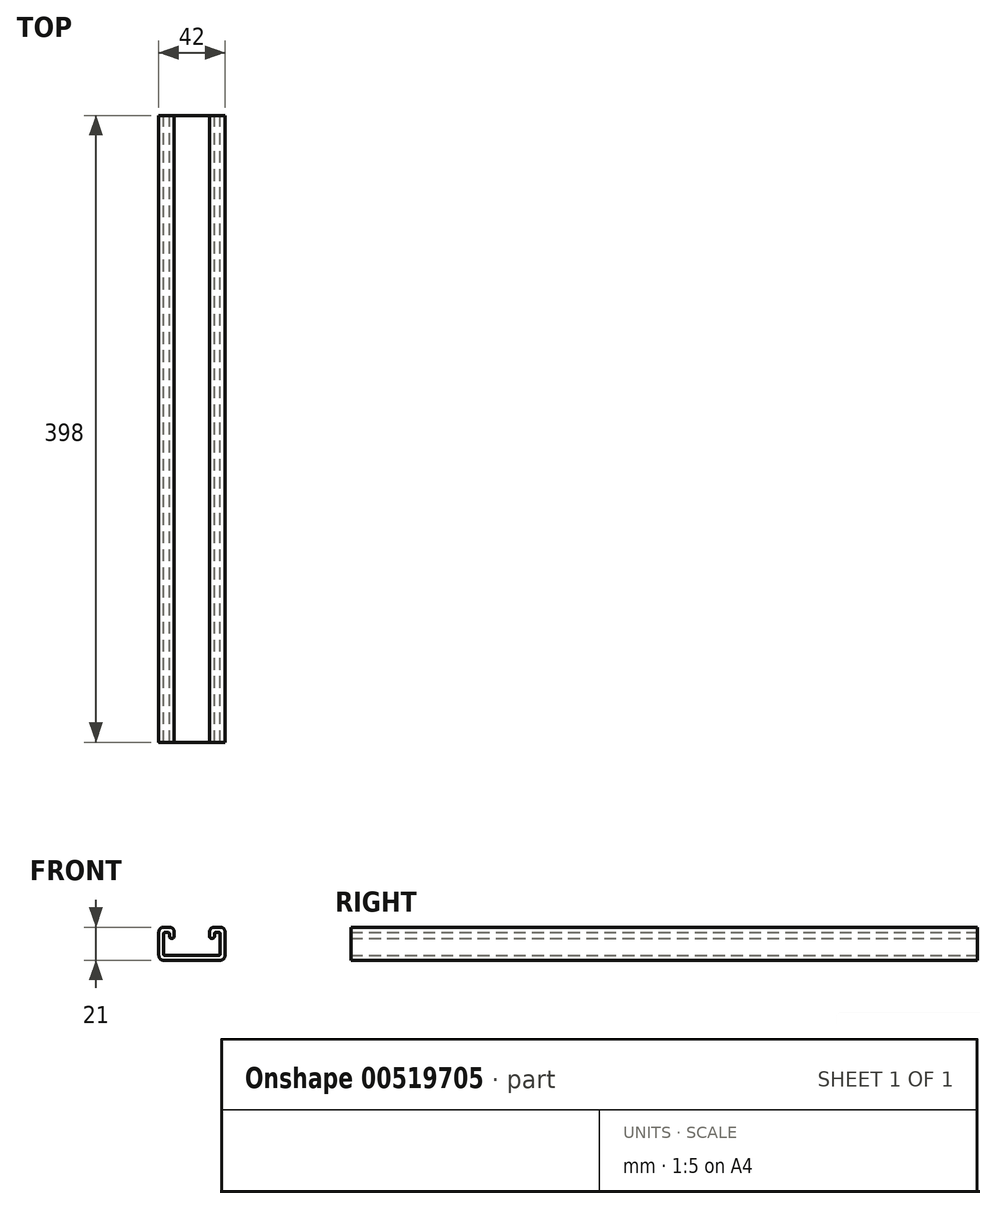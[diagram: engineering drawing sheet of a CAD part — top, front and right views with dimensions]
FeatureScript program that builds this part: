
annotation { "Feature Type Name" : "Feature", "Feature Type Description" : "" }
export const myFeature = defineFeature(function(context is Context, id is Id, definition is map)
    precondition{}
    {
        {
            var Q0;
            Q0=qCreatedBy(makeId("Front.planeOp"),FACE);
            var sketch = newSketch(context, id + "F0", { "sketchPlane" : qUnion([Q0])});
            skLineSegment(sketch, "E0.bottom", {"start": v(0, 0) * mm, "end": v(42, 0) * mm});
            skLineSegment(sketch, "E0.top", {"start": v(0, 21) * mm, "end": v(42, 21) * mm});
            skLineSegment(sketch, "E0.left", {"start": v(0, 0) * mm, "end": v(0, 21) * mm});
            skLineSegment(sketch, "E0.right", {"start": v(42, 0) * mm, "end": v(42, 21) * mm});
            skLineSegment(sketch, "E1.bottom", {"start": v(3, 3) * mm, "end": v(39, 3) * mm});
            skLineSegment(sketch, "E1.top", {"start": v(3, 14) * mm, "end": v(39, 14) * mm});
            skLineSegment(sketch, "E1.left", {"start": v(3, 3) * mm, "end": v(3, 14) * mm});
            skLineSegment(sketch, "E1.right", {"start": v(39, 3) * mm, "end": v(39, 14) * mm});
            skLineSegment(sketch, "E2.bottom", {"start": v(9.75, 21) * mm, "end": v(32.25, 21) * mm});
            skLineSegment(sketch, "E2.top", {"start": v(9.75, 14) * mm, "end": v(32.25, 14) * mm});
            skLineSegment(sketch, "E2.left", {"start": v(9.75, 21) * mm, "end": v(9.75, 14) * mm});
            skLineSegment(sketch, "E2.right", {"start": v(32.25, 21) * mm, "end": v(32.25, 14) * mm});
            skLineSegment(sketch, "E3.bottom", {"start": v(3.02, 17.75) * mm, "end": v(6.77, 17.75) * mm});
            skLineSegment(sketch, "E3.top", {"start": v(3.02, 14) * mm, "end": v(6.77, 14) * mm});
            skLineSegment(sketch, "E3.left", {"start": v(3.02, 17.75) * mm, "end": v(3.02, 14) * mm});
            skLineSegment(sketch, "E3.right", {"start": v(6.77, 17.75) * mm, "end": v(6.77, 14) * mm});
            skLineSegment(sketch, "E4.bottom", {"start": v(35.25, 17.75) * mm, "end": v(39, 17.75) * mm});
            skLineSegment(sketch, "E4.top", {"start": v(35.25, 14) * mm, "end": v(39, 14) * mm});
            skLineSegment(sketch, "E4.left", {"start": v(35.25, 17.75) * mm, "end": v(35.25, 14) * mm});
            skLineSegment(sketch, "E4.right", {"start": v(39, 17.75) * mm, "end": v(39, 14) * mm});
            skSolve(sketch);
        }
        {
            var Q0;
            Q0=makeQuery(id+"F0.imprint","IMPRINT",FACE,{"disambiguationData":[TD([[makeQuery(id+"F0.imprint","IMPRINT",EDGE,{"derivedFrom":sQuery(id+"F0.wireOp",EDGE,"E0.bottom")}),1.0]])]});
            extrude(context, id + "F1", {"entities" : qUnion([Q0]), "depth" : 398 * mm, "offsetDistance" : 25 * mm});
        }
        {
            var Q0;
            Q0=makeQuery(id+"F1.opExtrude","SWEPT_EDGE",EDGE,{"disambiguationData":[OSD([sQuery(id+"F0.wireOp",EDGE,"E0.top"),sQuery(id+"F0.wireOp",EDGE,"E0.left")])]});
            var Q1;
            Q1=makeQuery(id+"F1.opExtrude","SWEPT_EDGE",EDGE,{"disambiguationData":[OSD([sQuery(id+"F0.wireOp",EDGE,"E0.top"),sQuery(id+"F0.wireOp",EDGE,"E2.bottom"),sQuery(id+"F0.wireOp",EDGE,"E2.left")])]});
            var Q2;
            Q2=makeQuery(id+"F1.opExtrude","SWEPT_EDGE",EDGE,{"disambiguationData":[OSD([sQuery(id+"F0.wireOp",EDGE,"E0.top"),sQuery(id+"F0.wireOp",EDGE,"E2.bottom"),sQuery(id+"F0.wireOp",EDGE,"E2.right")])]});
            var Q3;
            Q3=makeQuery(id+"F1.opExtrude","SWEPT_EDGE",EDGE,{"disambiguationData":[OSD([sQuery(id+"F0.wireOp",EDGE,"E0.top"),sQuery(id+"F0.wireOp",EDGE,"E0.right")])]});
            var Q4;
            Q4=makeQuery(id+"F1.opExtrude","SWEPT_EDGE",EDGE,{"disambiguationData":[OSD([sQuery(id+"F0.wireOp",EDGE,"E0.bottom"),sQuery(id+"F0.wireOp",EDGE,"E0.left")])]});
            var Q5;
            Q5=makeQuery(id+"F1.opExtrude","SWEPT_EDGE",EDGE,{"disambiguationData":[OSD([sQuery(id+"F0.wireOp",EDGE,"E0.bottom"),sQuery(id+"F0.wireOp",EDGE,"E0.right")])]});
            fillet(context, id + "F2", {"entities" : qUnion([Q0, Q1, Q2, Q3, Q4, Q5]), "radius" : 3 * mm, "tangentPropagation" : true, "allowEdgeOverflow" : false});
        }
        {
            var Q0;
            Q0=makeQuery(id+"F1.opExtrude","SWEPT_EDGE",EDGE,{"disambiguationData":[OSD([sQuery(id+"F0.wireOp",EDGE,"E1.top"),sQuery(id+"F0.wireOp",EDGE,"E3.top"),sQuery(id+"F0.wireOp",EDGE,"E3.right")])]});
            var Q1;
            Q1=makeQuery(id+"F1.opExtrude","SWEPT_EDGE",EDGE,{"disambiguationData":[OSD([sQuery(id+"F0.wireOp",EDGE,"E1.top"),sQuery(id+"F0.wireOp",EDGE,"E2.top"),sQuery(id+"F0.wireOp",EDGE,"E2.right")])]});
            var Q2;
            Q2=makeQuery(id+"F1.opExtrude","SWEPT_EDGE",EDGE,{"disambiguationData":[OSD([sQuery(id+"F0.wireOp",EDGE,"E1.top"),sQuery(id+"F0.wireOp",EDGE,"E4.top"),sQuery(id+"F0.wireOp",EDGE,"E4.left")])]});
            var Q3;
            Q3=makeQuery(id+"F1.opExtrude","SWEPT_EDGE",EDGE,{"disambiguationData":[OSD([sQuery(id+"F0.wireOp",EDGE,"E1.top"),sQuery(id+"F0.wireOp",EDGE,"E2.top"),sQuery(id+"F0.wireOp",EDGE,"E2.left")])]});
            var Q4;
            Q4=makeQuery(id+"F1.opExtrude","SWEPT_EDGE",EDGE,{"disambiguationData":[OSD([sQuery(id+"F0.wireOp",EDGE,"E1.bottom"),sQuery(id+"F0.wireOp",EDGE,"E1.left")])]});
            var Q5;
            Q5=makeQuery(id+"F1.opExtrude","SWEPT_EDGE",EDGE,{"disambiguationData":[OSD([sQuery(id+"F0.wireOp",EDGE,"E1.bottom"),sQuery(id+"F0.wireOp",EDGE,"E1.right")])]});
            var Q6;
            Q6=makeQuery(id+"F1.opExtrude","SWEPT_EDGE",EDGE,{"disambiguationData":[OSD([sQuery(id+"F0.wireOp",EDGE,"E4.bottom"),sQuery(id+"F0.wireOp",EDGE,"E4.right")])]});
            var Q7;
            Q7=makeQuery(id+"F1.opExtrude","SWEPT_EDGE",EDGE,{"disambiguationData":[OSD([sQuery(id+"F0.wireOp",EDGE,"E3.bottom"),sQuery(id+"F0.wireOp",EDGE,"E3.left")])]});
            var Q8;
            Q8=makeQuery(id+"F1.opExtrude","SWEPT_EDGE",EDGE,{"disambiguationData":[OSD([sQuery(id+"F0.wireOp",EDGE,"E4.bottom"),sQuery(id+"F0.wireOp",EDGE,"E4.left")])]});
            var Q9;
            Q9=makeQuery(id+"F1.opExtrude","SWEPT_EDGE",EDGE,{"disambiguationData":[OSD([sQuery(id+"F0.wireOp",EDGE,"E3.bottom"),sQuery(id+"F0.wireOp",EDGE,"E3.right")])]});
            fillet(context, id + "F3", {"entities" : qUnion([Q0, Q1, Q2, Q3, Q4, Q5, Q6, Q7, Q8, Q9]), "radius" : 1 * mm, "tangentPropagation" : true, "allowEdgeOverflow" : false});
        }
    });
